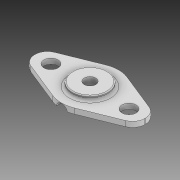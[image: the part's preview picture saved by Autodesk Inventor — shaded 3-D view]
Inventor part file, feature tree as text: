
AUTODESK INVENTOR PART (.ipt)
format: ipt  version: 2020 (Build 240168000, 168)  size: 320,000 bytes
history: native  units: mm
features: other x7, sketch x4, extrude x3, revolve x2, fillet x1, imported_body x1
ambient origin geometry x8: Origin, YZ Plane, XZ Plane, XY Plane, X Axis, Y Axis, Z Axis, Center Point
bodies: Solid1 (feature_tree)
feature tree (18):
  other  "HD_mastersketch.ipt"
  other  "Blocks"
  revolve  "Revolution1"  [1 undecoded]
  extrude  "Extrusion1"  Depth=10.0mm
  extrude  "Extrusion2"  TaperAngle=0.0deg  [1 undecoded]
  fillet  "Fillet1"  [1 undecoded]
  extrude  "Extrusion3"  Depth=10.0mm
  revolve  "Revolution2"  [1 undecoded]
  other  "608 bearing"
  other  "Belt"
  other  "Rotor"
  imported_body  "Base"
  sketch  "Sketch8"  dims[d1=10.0mm d24=7.0mm d25=22.0mm d26=8.0mm]
  sketch  "Sketch9"  dims[d2=90.0deg d3=5.0mm d4=10.0mm]
  sketch  "Sketch10"  dims[d5=15.0mm d6=0.0mm d7=0.0mm d8=0.0mm d9=0.0mm]
  sketch  "Sketch14"  dims[d10=7.0mm d11=2.775mm d12=2.3mm d13=5.7mm d14=5.7mm d15=0.0mm d29=1.65mm d30=3.0mm d32=10.0mm d33=1.5mm d34=90.0deg d36=4.0mm d38=3.25mm]
  other  "608 bearing:1"
  other  "608 bearing:2"
note: 4 required parameter values undecoded (feature->parameter linkage not recoverable at this tier; creation-order binding heuristic only, values carry confidence <= 0.55)